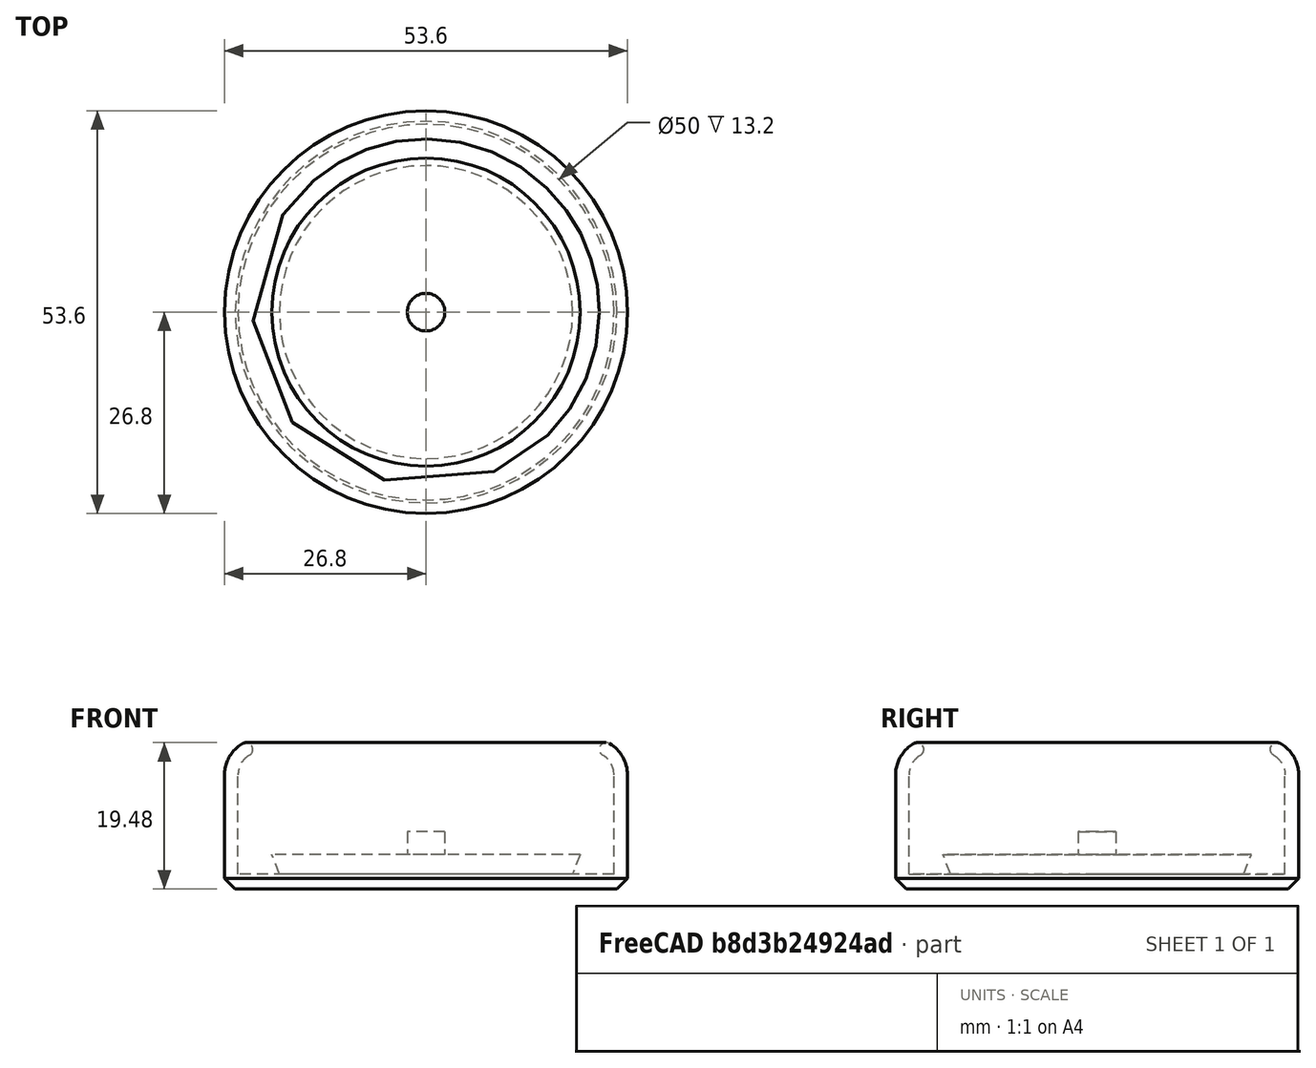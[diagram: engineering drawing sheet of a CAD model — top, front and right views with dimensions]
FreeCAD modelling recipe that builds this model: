
FCSTD DOCUMENT  (FreeCAD 2021.1015R24301 +3962 (Git))
Label: nogica
License: All rights reserved
LicenseURL: http://en.wikipedia.org/wiki/All_rights_reserved
objects: Sketcher::SketchObject×1, PartDesign::Revolution×1, PartDesign::Body×1
note: 5 computed .brp shape members not serialized (recipe doc carries the construction recipe); baked Part::Feature solids carry a one-line shape summary decoded from their .brp

FEATURE [Sketcher::SketchObject] Sketch
  FullyConstrained = true
  MapMode = 5
  Placement = pos=(0,0,0) rot=(1,0,0;1.5708rad)
  Support = -> [XZ_Plane]
  expr: Constraints[15] = 39mm / 2
  sketch-geometry (14):
    g0: LineSegment StartX=0 StartY=5.6 StartZ=0 EndX=2.5 EndY=5.6 EndZ=0
    g1: LineSegment StartX=2.5 StartY=5.6 StartZ=0 EndX=2.5 EndY=2.6 EndZ=0
    g2: LineSegment StartX=2.5 StartY=2.6 StartZ=0 EndX=20.5 EndY=2.6 EndZ=0
    g3: LineSegment StartX=20.5 StartY=2.6 StartZ=0 EndX=19.5 EndY=0 EndZ=0
    g4: LineSegment StartX=19.5 StartY=0 StartZ=0 EndX=25 EndY=0 EndZ=0
    g5: LineSegment StartX=25 StartY=0 StartZ=0 EndX=25 EndY=13.2 EndZ=0
    g6: ArcOfCircle CenterX=22 CenterY=13.2 CenterZ=0 NormalX=0 NormalY=0 NormalZ=1 AngleXU=0 Radius=3 StartAngle=0 EndAngle=1.0472
    g7: LineSegment StartX=0 StartY=5.6 StartZ=0 EndX=0 EndY=-2 EndZ=0
    g8: LineSegment StartX=0 StartY=-2 StartZ=0 EndX=25.3858 EndY=-2 EndZ=0
    g9: LineSegment StartX=26.8 StartY=-0.585786 StartZ=0 EndX=26.8 EndY=13.2 EndZ=0
    g10: ArcOfCircle CenterX=22 CenterY=13.2 CenterZ=0 NormalX=0 NormalY=0 NormalZ=1 AngleXU=0 Radius=4.8 StartAngle=0 EndAngle=1.04719
    g11: ArcOfCircle CenterX=23.95 CenterY=16.5775 CenterZ=0 NormalX=0 NormalY=0 NormalZ=1 AngleXU=0 Radius=0.9 StartAngle=1.04719 EndAngle=4.18878
    g12: LineSegment StartX=25.3858 StartY=-2 StartZ=0 EndX=26.8 EndY=-0.585786 EndZ=0
    g13: ArcOfCircle [constr] CenterX=22 CenterY=13.2 CenterZ=0 NormalX=0 NormalY=0 NormalZ=1 AngleXU=0 Radius=3 StartAngle=0 EndAngle=1.5708
  constraints (42):
    c: PointOnObject(g0,g-2)
    c: Horizontal(g0)
    c: Coincident(g0,g1)
    c: Coincident(g1,g2)
    c: Horizontal(g2)
    c: Coincident(g2,g3)
    c: PointOnObject(g3,g-1)
    c: Coincident(g3,g4)
    c: PointOnObject(g4,g-1)
    c: Coincident(g4,g5)
    c: Vertical(g5)
    c: Tangent(g5,g6) = -1.5708
    c: DistanceX(g0,g0) = 2.5
    c: Vertical(g1)
    c: DistanceY(g1,g1) = 3
    c: DistanceX(g3) = 19.5
    c: DistanceY(g1) = 2.6
    c: DistanceX(g3,g2) = 1
    c: DistanceX(g4) = 25
    c: Radius(g6) = 3
    c: Coincident(g0,g7)
    c: Vertical(g7)
    c: Coincident(g7,g8)
    c: Horizontal(g8)
    c: Vertical(g9)
    c: Tangent(g9,g10) = -1.5708
    c: Coincident(g6,g10)
    c: DistanceX(g5,g9) = 1.8
    c: Coincident(g11,g6)
    c: Coincident(g11,g10)
    c: Tangent(g11,g10)
    c: Tangent(g11,g6)
    c: Coincident(g9,g12)
    c: Coincident(g8,g12)
    c: Angle(g12) = 0.785398
    c: Distance(g12) = 2
    c: DistanceY(g8,g4) = 2
    c: Coincident(g13,g6)
    c: Coincident(g13,g5)
    c: Vertical(g13,g6)
    c: DistanceY(g4,g13) = 16.2
    c: Angle(g6) = 1.0472
FEATURE [PartDesign::Revolution] Revolution
  Angle = 360
  Axis = (0,2e-16,1)
  Base = (0,0,0)
  ClaimChildren = false
  Fit = 0
  FitJoin = 0
  InnerFit = 0
  InnerFitJoin = 0
  NewSolid = false
  Placement = pos=(0,0,0) rot=(1,0,0;1.5708rad)
  Profile = -> Sketch
  ReferenceAxis = -> Sketch [V_Axis]
  Refine = true
  Reversed = true
  Suppress = false
  _ProfileBasedVersion = 1
FEATURE [PartDesign::Body] Body
  AutoGroupSolids = false
  ExportMode = 0
  Group = -> [Sketch,Revolution]
  Origin = -> Origin
  Tip = -> Revolution
  _ExportChildren = -> [Revolution]
  _GroupVersion = 1
